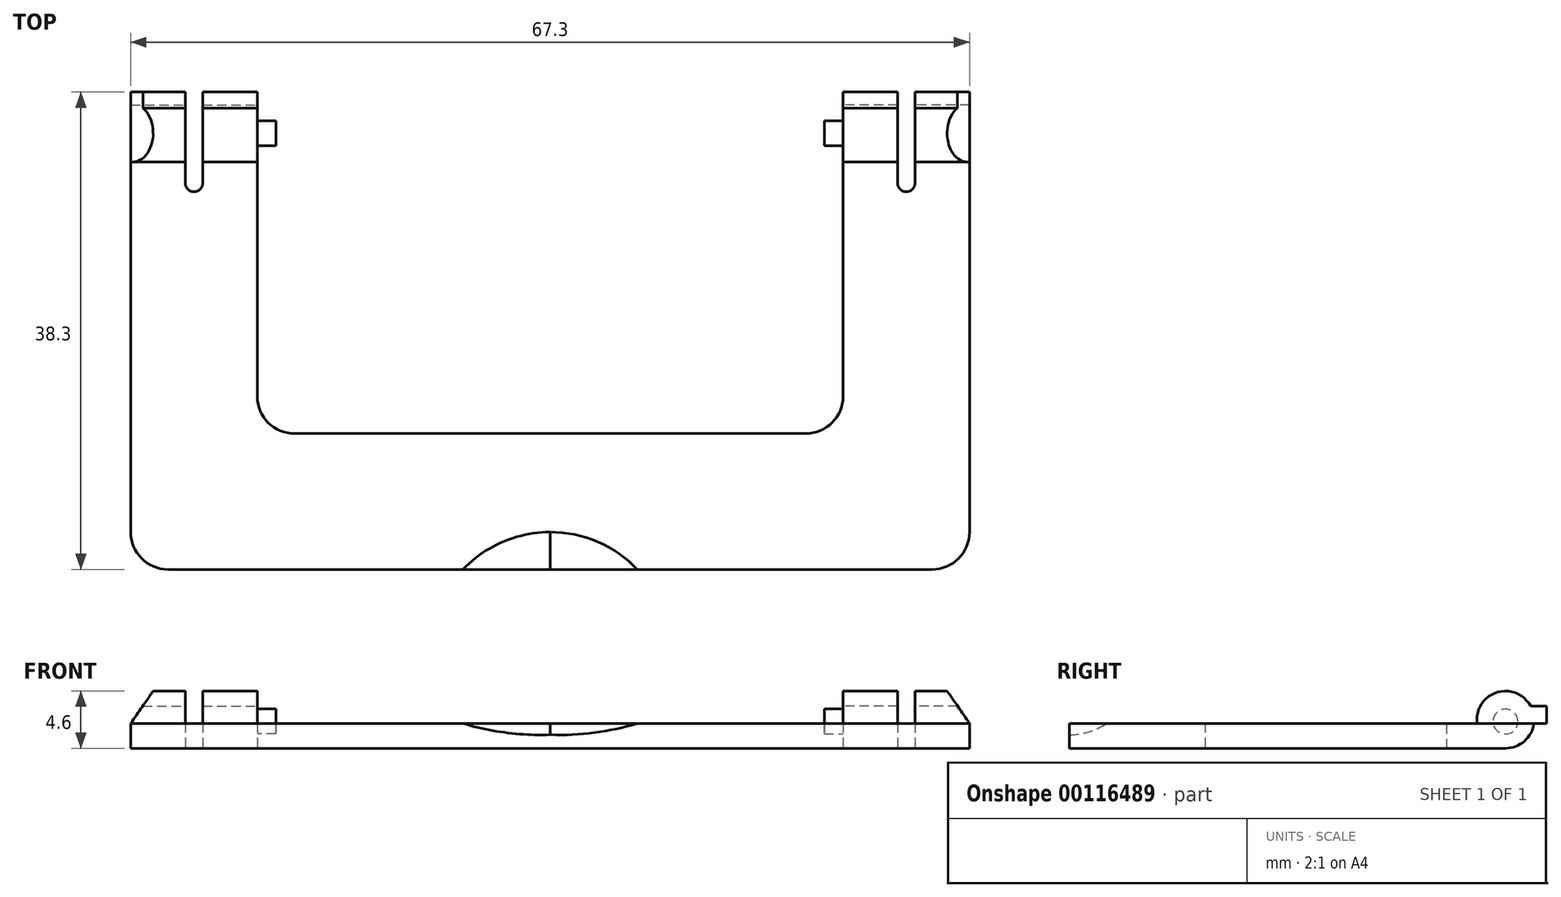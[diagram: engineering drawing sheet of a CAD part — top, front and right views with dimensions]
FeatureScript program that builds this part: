
annotation { "Feature Type Name" : "Feature", "Feature Type Description" : "" }
export const myFeature = defineFeature(function(context is Context, id is Id, definition is map)
    precondition{}
    {
        {
            var Q0;
            Q0=qCreatedBy(makeId("Top.planeOp"),FACE);
            var sketch = newSketch(context, id + "F0", { "sketchPlane" : qUnion([Q0])});
            skLineSegment(sketch, "E0", {"start": v(0, 0) * mm, "end": v(33.65, 0) * mm});
            skLineSegment(sketch, "E1", {"start": v(33.65, 0) * mm, "end": v(33.65, 35) * mm});
            skLineSegment(sketch, "E2", {"start": v(33.65, 35) * mm, "end": v(23.5, 35) * mm});
            skLineSegment(sketch, "E3", {"start": v(23.5, 35) * mm, "end": v(23.5, 10.9) * mm});
            skLineSegment(sketch, "E4", {"start": v(23.5, 10.9) * mm, "end": v(0, 10.9) * mm});
            skLineSegment(sketch, "E5", {"start": v(0, 10.9) * mm, "end": v(0, 0) * mm});
            skSolve(sketch);
        }
        {
            var Q0;
            Q0=makeQuery(id+"F0.imprint","IMPRINT",FACE,{"disambiguationData":[TD([[makeQuery(id+"F0.imprint","IMPRINT",EDGE,{"derivedFrom":sQuery(id+"F0.wireOp",EDGE,"E0")}),1.0]])]});
            extrude(context, id + "F1", {"entities" : qUnion([Q0]), "depth" : 2 * mm});
        }
        {
            var Q0;
            Q0=makeQuery(id+"F1.opExtrude","SWEPT_EDGE",EDGE,{"disambiguationData":[OSD([sQuery(id+"F0.wireOp",EDGE,"E0"),sQuery(id+"F0.wireOp",EDGE,"E1")])]});
            var Q1;
            Q1=makeQuery(id+"F1.opExtrude","SWEPT_EDGE",EDGE,{"disambiguationData":[OSD([sQuery(id+"F0.wireOp",EDGE,"E3"),sQuery(id+"F0.wireOp",EDGE,"E4")])]});
            fillet(context, id + "F2", {"entities" : qUnion([Q0, Q1]), "radius" : 3 * mm, "tangentPropagation" : true, "allowEdgeOverflow" : false});
        }
        {
            var Q0;
            {var subQ0=makeQuery(id+"F1.opExtrude","CAP_FACE",FACE,{"disambiguationData":[OSD([sQuery(id+"F0.wireOp",EDGE,"E0"),sQuery(id+"F0.wireOp",EDGE,"E1"),sQuery(id+"F0.wireOp",EDGE,"E2"),sQuery(id+"F0.wireOp",EDGE,"E3"),sQuery(id+"F0.wireOp",EDGE,"E4"),sQuery(id+"F0.wireOp",EDGE,"E5")])],"isStart":false});Q0=makeQuery(id+"F20.boolean.opBoolean","MERGE",FACE,{"derivedFrom":[subQ0,makeQuery(id+"F20.opPattern","COPY",FACE,{"derivedFrom":subQ0,"instanceName":"1"})]});}
            cPlane(context, id + "F3", {"entities" : qUnion([Q0]), "cplaneType" : CPlaneType.OFFSET, "offset" : 0 * mm, "width" : 150 * mm, "height" : 150 * mm});
        }
        {
            var Q0;
            Q0=qCreatedBy(id+"F3.planeOp",FACE);
            var sketch = newSketch(context, id + "F4", { "sketchPlane" : qUnion([Q0])});
            skLineSegment(sketch, "E6", {"start": v(0, 0) * mm, "end": v(7, 0) * mm});
            skLineSegment(sketch, "E7", {"start": v(0, 0) * mm, "end": v(0, 3) * mm});
            skArc(sketch, "E8", {"start": v(7, 0) * mm, "mid": v(3.8, 2.22) * mm, "end": v(0, 3) * mm});
            skSolve(sketch);
        }
        {
            var Q0;
            Q0=qCreatedBy(makeId("Right.planeOp"),FACE);
            var sketch = newSketch(context, id + "F5", { "sketchPlane" : qUnion([Q0])});
            skLineSegment(sketch, "E9", {"start": v(0, 2) * mm, "end": v(0, 1.09) * mm});
            skArc(sketch, "E10", {"start": v(0, 1.09) * mm, "mid": v(1.57, 1.32) * mm, "end": v(3, 2) * mm});
            skSolve(sketch);
        }
        {
            var Q0;
            Q0=qCreatedBy(makeId("Front.planeOp"),FACE);
            var sketch = newSketch(context, id + "F6", { "sketchPlane" : qUnion([Q0])});
            skPoint(sketch, "E11.0", {"position": v(0, 2) * mm});
            skPoint(sketch, "E12.0", {"position": v(7, 2) * mm});
            skPoint(sketch, "E13.0", {"position": v(0, 1.09) * mm});
            skLineSegment(sketch, "E14", {"start": v(0, 2) * mm, "end": v(0, 1.09) * mm});
            skLineSegment(sketch, "E15", {"start": v(0, 2) * mm, "end": v(7, 2) * mm});
            skArc(sketch, "E16", {"start": v(0, 1.09) * mm, "mid": v(3.54, 1.26) * mm, "end": v(7, 2) * mm});
            skSolve(sketch);
        }
        {
            var Q0;
            Q0=makeQuery(id+"F1.opExtrude","SWEPT_FACE",FACE,{"disambiguationData":[OSD([sQuery(id+"F0.wireOp",EDGE,"E3")])]});
            cPlane(context, id + "F7", {"entities" : qUnion([Q0]), "cplaneType" : CPlaneType.OFFSET, "offset" : 0 * mm, "width" : 150 * mm, "height" : 150 * mm});
        }
        {
            var Q0;
            Q0=qCreatedBy(id+"F7.planeOp",FACE);
            var sketch = newSketch(context, id + "F8", { "sketchPlane" : qUnion([Q0])});
            skPoint(sketch, "E17.0", {"position": v(-35, 2) * mm});
            skPoint(sketch, "E18.0", {"position": v(-35, 0) * mm});
            skLineSegment(sketch, "E19", {"start": v(-35, 0) * mm, "end": v(-35, 2.15) * mm, "construction": true});
            skCircle(sketch, "E20", {"center": v(-35, 2.15) * mm, "radius": 2.15 * mm});
            skSolve(sketch);
        }
        {
            var Q0;
            Q0=qCreatedBy(id+"F7.planeOp",FACE);
            var sketch = newSketch(context, id + "F9", { "sketchPlane" : qUnion([Q0])});
            skPoint(sketch, "E21.0", {"position": v(-35, 2.15) * mm});
            skCircle(sketch, "E22", {"center": v(-35, 2.15) * mm, "radius": 1 * mm});
            skSolve(sketch);
        }
        {
            var Q0;
            Q0=makeQuery(id+"F9.imprint","IMPRINT",FACE,{"disambiguationData":[TD([[makeQuery(id+"F9.imprint","IMPRINT",EDGE,{"derivedFrom":sQuery(id+"F9.wireOp",EDGE,"E22")}),1.0]])]});
            extrude(context, id + "F10", {"entities" : qUnion([Q0]), "operationType" : NewBodyOperationType.ADD, "depth" : 1.5 * mm});
        }
        {
            var Q0;
            Q0=qCreatedBy(id+"F7.planeOp",FACE);
            var sketch = newSketch(context, id + "F11", { "sketchPlane" : qUnion([Q0])});
            skPoint(sketch, "E23.0", {"position": v(-35, 0) * mm});
            skLineSegment(sketch, "E24", {"start": v(-35, 0) * mm, "end": v(-35, 2.3) * mm, "construction": true});
            skCircle(sketch, "E25", {"center": v(-35, 2.3) * mm, "radius": 2.3 * mm});
            skPoint(sketch, "E26.0", {"position": v(-35, 2) * mm});
            skLineSegment(sketch, "E27.right", {"start": v(-38.3, 2) * mm, "end": v(-38.3, 3.4) * mm});
            skLineSegment(sketch, "E28", {"start": v(-38.3, 2) * mm, "end": v(-37.28, 2) * mm});
            skLineSegment(sketch, "E29", {"start": v(-38.3, 3.4) * mm, "end": v(-37.02, 3.4) * mm});
            skSolve(sketch);
        }
        {
            var Q0;
            {var subQ0=sQuery(id+"F11.wireOp",EDGE,"E25");var subQ1=makeQuery(id+"F11.imprint","INTERSECT",VERTEX,{"derivedFrom":[subQ0,sQuery(id+"F11.wireOp",EDGE,"E28")]});Q0=makeQuery(id+"F11.imprint","IMPRINT",FACE,{"disambiguationData":[TD([[makeQuery(id+"F11.imprint","IMPRINT",EDGE,{"disambiguationData":[TD([[subQ1,1.0]])],"derivedFrom":subQ0}),1.0]])]});}
            var Q1;
            Q1=makeQuery(id+"F11.imprint","IMPRINT",FACE,{"disambiguationData":[TD([[makeQuery(id+"F11.imprint","IMPRINT",EDGE,{"derivedFrom":sQuery(id+"F11.wireOp",EDGE,"E27.right")}),-1.0]])]});
            var Q2;
            Q2=makeQuery(id+"F1.opExtrude","SWEPT_FACE",FACE,{"disambiguationData":[OSD([sQuery(id+"F0.wireOp",EDGE,"E1")])]});
            extrude(context, id + "F12", {"entities" : qUnion([Q0, Q1]), "operationType" : NewBodyOperationType.ADD, "endBound" : BoundingType.UP_TO_SURFACE, "oppositeDirection" : true, "endBoundEntityFace" : qUnion([Q2]), "depth" : 25 * mm});
        }
        {
            var Q0;
            Q0=qCreatedBy(makeId("Front.planeOp"),FACE);
            var sketch = newSketch(context, id + "F13", { "sketchPlane" : qUnion([Q0])});
            skPoint(sketch, "E30.0", {"position": v(33.65, 2) * mm});
            skLineSegment(sketch, "E31.0", {"start": v(33.65, 4.6) * mm, "end": v(33.65, 2) * mm});
            skLineSegment(sketch, "E32", {"start": v(33.65, 4.6) * mm, "end": v(31.85, 4.6) * mm});
            skLineSegment(sketch, "E33", {"start": v(31.85, 4.6) * mm, "end": v(33.65, 2) * mm});
            skSolve(sketch);
        }
        {
            var Q0;
            Q0=makeQuery(id+"F13.imprint","IMPRINT",FACE,{"disambiguationData":[TD([[makeQuery(id+"F13.imprint","IMPRINT",EDGE,{"derivedFrom":sQuery(id+"F13.wireOp",EDGE,"E31.0")}),-1.0]])]});
            extrude(context, id + "F14", {"entities" : qUnion([Q0]), "operationType" : NewBodyOperationType.REMOVE, "endBound" : BoundingType.THROUGH_ALL, "oppositeDirection" : true, "depth" : 25 * mm});
        }
        {
            var Q0;
            Q0=makeQuery(id+"F12.opExtrude","SWEPT_EDGE",EDGE,{"disambiguationData":[OSD([sQuery(id+"F11.wireOp",EDGE,"E27.right"),sQuery(id+"F11.wireOp",EDGE,"E28")])]});
            cPlane(context, id + "F15", {"entities" : qUnion([Q0]), "cplaneType" : CPlaneType.MID_PLANE, "offset" : 25 * mm, "width" : 150 * mm, "height" : 150 * mm});
        }
        {
            var Q0;
            Q0=qCreatedBy(id+"F15.planeOp",FACE);
            var sketch = newSketch(context, id + "F16", { "sketchPlane" : qUnion([Q0])});
            skPoint(sketch, "E34.0", {"position": v(-38.3, 3.4) * mm});
            skCircle(sketch, "E35.0", {"center": v(-35, 2.3) * mm, "radius": 2.3 * mm});
            skLineSegment(sketch, "E36.bottom", {"start": v(-38.3, 4.6) * mm, "end": v(-30.3, 4.6) * mm});
            skLineSegment(sketch, "E36.top", {"start": v(-38.3, 0) * mm, "end": v(-30.3, 0) * mm});
            skLineSegment(sketch, "E36.left", {"start": v(-38.3, 4.6) * mm, "end": v(-38.3, 0) * mm});
            skLineSegment(sketch, "E36.right", {"start": v(-30.3, 4.6) * mm, "end": v(-30.3, 0) * mm});
            skSolve(sketch);
        }
        {
            var Q0;
            {var subQ5=sQuery(id+"F16.wireOp",EDGE,"E36.left");Q0=makeQuery(id+"F16.imprint","IMPRINT",FACE,{"disambiguationData":[TD([[makeQuery(id+"F16.imprint","IMPRINT",EDGE,{"derivedFrom":subQ5}),1.0]])]});}
            var Q1;
            {var subQ0=sQuery(id+"F16.wireOp",EDGE,"E35.0");var subQ1=makeQuery(id+"F16.imprint","INTERSECT",VERTEX,{"derivedFrom":[subQ0,sQuery(id+"F16.wireOp",EDGE,"E36.bottom")]});Q1=makeQuery(id+"F16.imprint","IMPRINT",FACE,{"disambiguationData":[TD([[makeQuery(id+"F16.imprint","IMPRINT",EDGE,{"disambiguationData":[TD([[subQ1,-1.0]])],"derivedFrom":subQ0}),1.0]])]});}
            var Q2;
            {var subQ5=sQuery(id+"F16.wireOp",EDGE,"E36.right");Q2=makeQuery(id+"F16.imprint","IMPRINT",FACE,{"disambiguationData":[TD([[makeQuery(id+"F16.imprint","IMPRINT",EDGE,{"derivedFrom":subQ5}),-1.0]])]});}
            extrude(context, id + "F17", {"entities" : qUnion([Q0, Q1, Q2]), "operationType" : NewBodyOperationType.REMOVE, "depth" : 1.4 * mm, "symmetric" : true});
        }
        {
            var Q0;
            Q0=makeQuery(id+"F17.boolean.opBoolean","COPY",EDGE,{"derivedFrom":makeQuery(id+"F17.opExtrude","CAP_EDGE",EDGE,{"disambiguationData":[OSD([sQuery(id+"F16.wireOp",EDGE,"E36.right")])],"isStart":false})});
            var Q1;
            Q1=makeQuery(id+"F17.boolean.opBoolean","COPY",EDGE,{"derivedFrom":makeQuery(id+"F17.opExtrude","CAP_EDGE",EDGE,{"disambiguationData":[OSD([sQuery(id+"F16.wireOp",EDGE,"E36.right")])],"isStart":true})});
            fillet(context, id + "F18", {"entities" : qUnion([Q0, Q1]), "radius" : 0.7 * mm, "tangentPropagation" : true, "allowEdgeOverflow" : false});
        }
        {
            var Q1;
            Q1=makeQuery(id+"F4.imprint","IMPRINT",FACE,{"disambiguationData":[TD([[makeQuery(id+"F4.imprint","IMPRINT",EDGE,{"derivedFrom":sQuery(id+"F4.wireOp",EDGE,"E6")}),1.0]])]});
            var Q2;
            Q2=makeQuery(id+"F6.imprint","IMPRINT",FACE,{"disambiguationData":[TD([[makeQuery(id+"F6.imprint","IMPRINT",EDGE,{"derivedFrom":sQuery(id+"F6.wireOp",EDGE,"E14")}),1.0]])]});
            var Q3;
            Q3=sQuery(id+"F5.wireOp",EDGE,"E10");
            loft(context, id + "F19", {"operationType" : NewBodyOperationType.REMOVE, "addGuides" : true, "sheetProfilesArray" : [{ "sheetProfileEntities" : qUnion([Q1]) }, { "sheetProfileEntities" : qUnion([Q2]) }], "guidesArray" : [{ "guideEntities" : qUnion([Q3]), "guideDerivativeType" : LoftGuideDerivativeType.DEFAULT, "guideDerivativeMagnitude" : 1 }]});
        }
        {
            var Q0;
            Q0=makeQuery(id+"F1.opExtrude","SWEPT_BODY",BODY,{"disambiguationData":[OSD([sQuery(id+"F0.wireOp",EDGE,"E0"),sQuery(id+"F0.wireOp",EDGE,"E1"),sQuery(id+"F0.wireOp",EDGE,"E2"),sQuery(id+"F0.wireOp",EDGE,"E3"),sQuery(id+"F0.wireOp",EDGE,"E4"),sQuery(id+"F0.wireOp",EDGE,"E5")])]});
            var Q1;
            Q1=makeQuery(id+"F1.opExtrude","SWEPT_FACE",FACE,{"disambiguationData":[OSD([sQuery(id+"F0.wireOp",EDGE,"E5")])]});
            var Q2;
            Q2=qCreatedBy(makeId("Right.planeOp"),FACE);
            mirror(context, id + "F20", {"operationType" : NewBodyOperationType.ADD, "entities" : qUnion([Q0]), "faces" : qUnion([Q1]), "mirrorPlane" : qUnion([Q2])});
        }
    });
